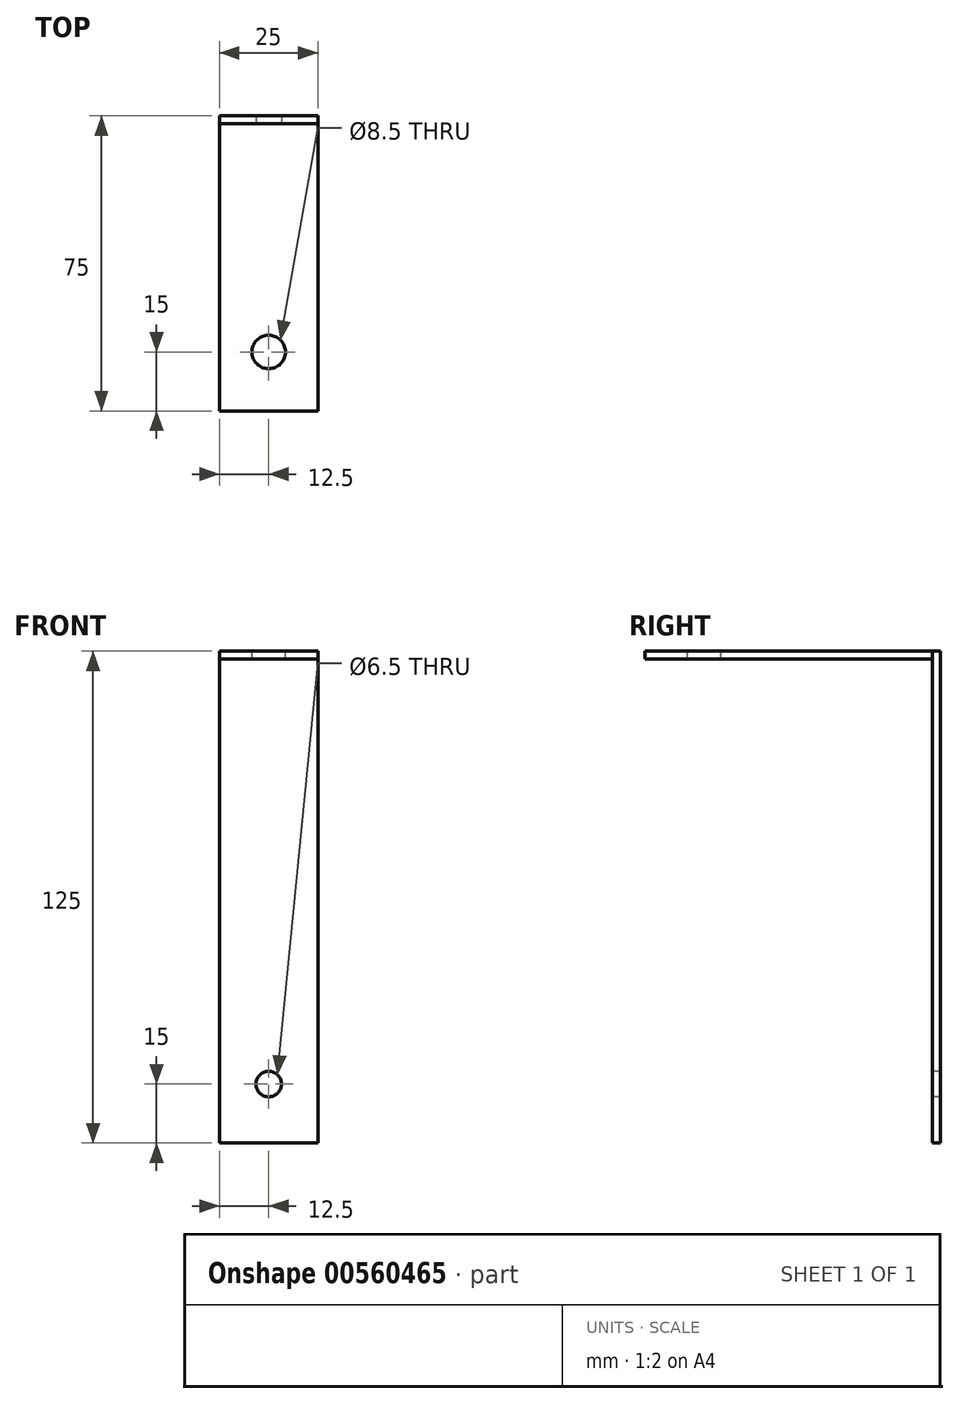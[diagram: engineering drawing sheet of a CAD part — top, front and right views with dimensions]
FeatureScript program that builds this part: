
annotation { "Feature Type Name" : "Feature", "Feature Type Description" : "" }
export const myFeature = defineFeature(function(context is Context, id is Id, definition is map)
    precondition{}
    {
        {
            var Q0;
            Q0=qCreatedBy(makeId("Front.planeOp"),FACE);
            var sketch = newSketch(context, id + "F0", { "sketchPlane" : qUnion([Q0])});
            skLineSegment(sketch, "E0.bottom", {"start": v(0, 0) * mm, "end": v(25, 0) * mm});
            skLineSegment(sketch, "E0.top", {"start": v(0, 125) * mm, "end": v(25, 125) * mm});
            skLineSegment(sketch, "E0.left", {"start": v(0, 0) * mm, "end": v(0, 125) * mm});
            skLineSegment(sketch, "E0.right", {"start": v(25, 0) * mm, "end": v(25, 125) * mm});
            skLineSegment(sketch, "E1", {"start": v(12.5, 0) * mm, "end": v(12.5, 15) * mm});
            skCircle(sketch, "E2", {"center": v(12.5, 15) * mm, "radius": 3.25 * mm});
            skSolve(sketch);
        }
        {
            var Q0;
            Q0 = qSketchRegion(id + "F0", true);
            extrude(context, id + "F1", {"entities" : qUnion([Q0]), "oppositeDirection" : true, "depth" : 2 * mm, "offsetDistance" : 25 * mm});
        }
        {
            var Q0;
            Q0=makeQuery(id+"F1.opExtrude","SWEPT_FACE",FACE,{"disambiguationData":[OSD([sQuery(id+"F0.wireOp",EDGE,"E0.left")])]});
            var sketch = newSketch(context, id + "F2", { "sketchPlane" : qUnion([Q0])});
            skLineSegment(sketch, "E3.bottom", {"start": v(0, 125) * mm, "end": v(73, 125) * mm});
            skLineSegment(sketch, "E3.top", {"start": v(0, 123) * mm, "end": v(73, 123) * mm});
            skLineSegment(sketch, "E3.left", {"start": v(0, 125) * mm, "end": v(0, 123) * mm});
            skLineSegment(sketch, "E3.right", {"start": v(73, 125) * mm, "end": v(73, 123) * mm});
            skSolve(sketch);
        }
        {
            var Q0;
            Q0 = qSketchRegion(id + "F2", true);
            extrude(context, id + "F3", {"entities" : qUnion([Q0]), "oppositeDirection" : true, "depth" : 25 * mm, "offsetDistance" : 25 * mm});
        }
        {
            var Q0;
            Q0=makeQuery(id+"F3.opExtrude","SWEPT_FACE",FACE,{"disambiguationData":[OSD([sQuery(id+"F2.wireOp",EDGE,"E3.bottom")])]});
            var sketch = newSketch(context, id + "F4", { "sketchPlane" : qUnion([Q0])});
            skCircle(sketch, "E4", {"center": v(12.5, -58) * mm, "radius": 4.25 * mm});
            skSolve(sketch);
        }
        {
            var Q0;
            Q0=makeQuery(id+"F4.imprint","IMPRINT",FACE,{"disambiguationData":[TD([[makeQuery(id+"F4.imprint","IMPRINT",EDGE,{"derivedFrom":sQuery(id+"F4.wireOp",EDGE,"E4")}),1.0]])]});
            extrude(context, id + "F5", {"entities" : qUnion([Q0]), "operationType" : NewBodyOperationType.REMOVE, "oppositeDirection" : true, "depth" : 2 * mm, "offsetDistance" : 25 * mm});
        }
    });
